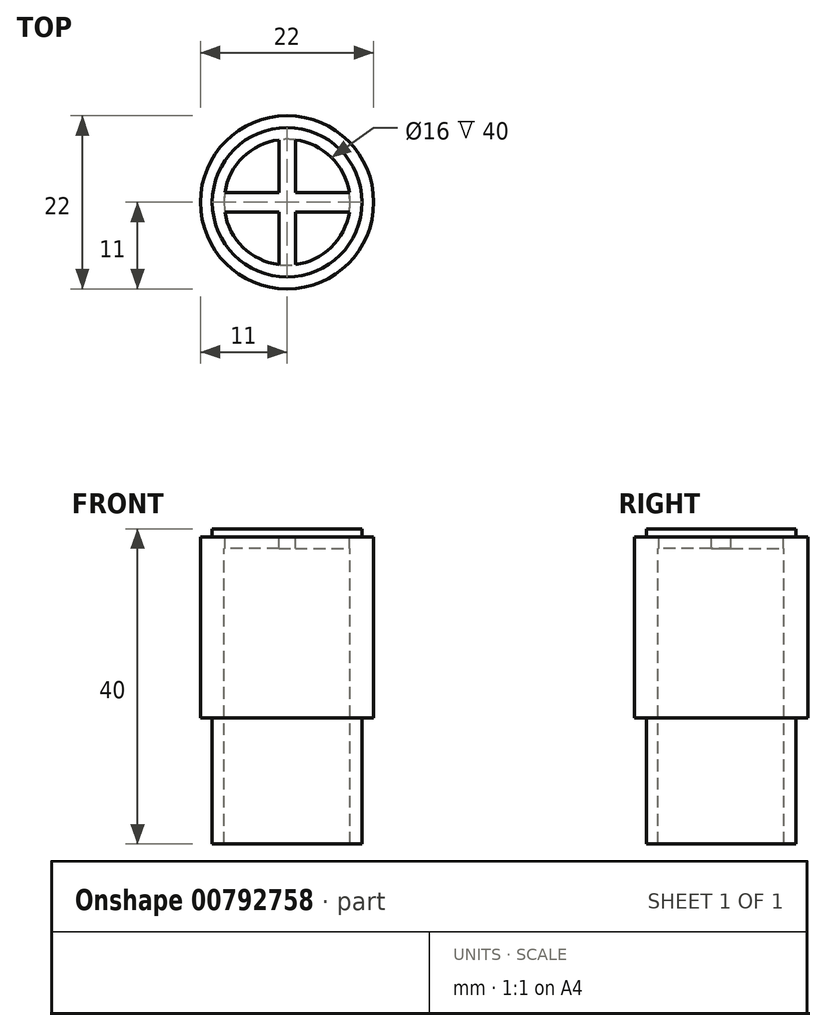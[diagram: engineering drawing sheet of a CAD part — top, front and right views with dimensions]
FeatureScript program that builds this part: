
annotation { "Feature Type Name" : "Feature", "Feature Type Description" : "" }
export const myFeature = defineFeature(function(context is Context, id is Id, definition is map)
    precondition{}
    {
        {
            var Q0;
            Q0=qCreatedBy(makeId("Top.planeOp"),FACE);
            var sketch = newSketch(context, id + "F0", { "sketchPlane" : qUnion([Q0])});
            skCircle(sketch, "E0", {"center": v(0, 0) * mm, "radius": 9.5 * mm});
            skSolve(sketch);
        }
        {
            var Q0;
            Q0 = qSketchRegion(id + "F0", true);
            extrude(context, id + "F1", {"entities" : qUnion([Q0]), "endBound" : BoundingType.SYMMETRIC, "depth" : 40 * mm, "offsetDistance" : 25 * mm});
        }
        {
            var Q0;
            Q0=makeQuery(id+"F1.opExtrude","CAP_FACE",FACE,{"disambiguationData":[OSD([sQuery(id+"F0.wireOp",EDGE,"E0")])],"isStart":false});
            var sketch = newSketch(context, id + "F2", { "sketchPlane" : qUnion([Q0])});
            skCircle(sketch, "E1", {"center": v(0, 0) * mm, "radius": 8 * mm});
            skCircle(sketch, "E2", {"center": v(0, 0) * mm, "radius": 1.63 * mm});
            skLineSegment(sketch, "E3", {"start": v(-1.05, 1.24) * mm, "end": v(-1.05, 7.93) * mm});
            skLineSegment(sketch, "E4", {"start": v(1.05, 1.24) * mm, "end": v(1.05, 7.93) * mm});
            skLineSegment(sketch, "E5", {"start": v(1.05, 1.24) * mm, "end": v(7.9, 1.24) * mm});
            skLineSegment(sketch, "E6", {"start": v(1.05, -1.24) * mm, "end": v(7.9, -1.24) * mm});
            skLineSegment(sketch, "E7", {"start": v(1.05, -1.24) * mm, "end": v(1.05, -7.93) * mm});
            skLineSegment(sketch, "E8", {"start": v(-1.05, -1.24) * mm, "end": v(-1.05, -7.93) * mm});
            skLineSegment(sketch, "E9", {"start": v(-1.05, 1.24) * mm, "end": v(-7.9, 1.24) * mm});
            skLineSegment(sketch, "E10", {"start": v(-1.05, -1.24) * mm, "end": v(-7.9, -1.24) * mm});
            skSolve(sketch);
        }
        {
            var Q0;
            {var subQ0=sQuery(id+"F2.wireOp",EDGE,"E3");Q0=makeQuery(id+"F2.imprint","IMPRINT",FACE,{"disambiguationData":[TD([[makeQuery(id+"F2.imprint","IMPRINT",EDGE,{"derivedFrom":subQ0}),1.0]])]});}
            var Q1;
            {var subQ0=sQuery(id+"F2.wireOp",EDGE,"E4");Q1=makeQuery(id+"F2.imprint","IMPRINT",FACE,{"disambiguationData":[TD([[makeQuery(id+"F2.imprint","IMPRINT",EDGE,{"derivedFrom":subQ0}),-1.0]])]});}
            var Q2;
            {var subQ0=sQuery(id+"F2.wireOp",EDGE,"E6");Q2=makeQuery(id+"F2.imprint","IMPRINT",FACE,{"disambiguationData":[TD([[makeQuery(id+"F2.imprint","IMPRINT",EDGE,{"derivedFrom":subQ0}),-1.0]])]});}
            var Q3;
            {var subQ0=sQuery(id+"F2.wireOp",EDGE,"E8");Q3=makeQuery(id+"F2.imprint","IMPRINT",FACE,{"disambiguationData":[TD([[makeQuery(id+"F2.imprint","IMPRINT",EDGE,{"derivedFrom":subQ0}),-1.0]])]});}
            extrude(context, id + "F3", {"entities" : qUnion([Q0, Q1, Q2, Q3]), "operationType" : NewBodyOperationType.REMOVE, "oppositeDirection" : true, "depth" : 50 * mm, "offsetDistance" : 25 * mm});
        }
        {
            var Q0;
            Q0=makeQuery(id+"F1.opExtrude","CAP_FACE",FACE,{"disambiguationData":[OSD([sQuery(id+"F0.wireOp",EDGE,"E0")])],"isStart":false});
            var sketch = newSketch(context, id + "F4", { "sketchPlane" : qUnion([Q0])});
            skLineSegment(sketch, "E11", {"start": v(-1.05, 1.24) * mm, "end": v(-1.05, 7.93) * mm});
            skLineSegment(sketch, "E12", {"start": v(1.05, 1.24) * mm, "end": v(1.05, 7.93) * mm});
            skLineSegment(sketch, "E13", {"start": v(1.05, 1.24) * mm, "end": v(7.9, 1.24) * mm});
            skLineSegment(sketch, "E14", {"start": v(1.05, -1.24) * mm, "end": v(7.9, -1.24) * mm});
            skLineSegment(sketch, "E15", {"start": v(1.05, -1.24) * mm, "end": v(1.05, -7.93) * mm});
            skLineSegment(sketch, "E16", {"start": v(-1.05, -1.24) * mm, "end": v(-1.05, -7.93) * mm});
            skLineSegment(sketch, "E17", {"start": v(-1.05, -1.24) * mm, "end": v(-7.9, -1.24) * mm});
            skLineSegment(sketch, "E18", {"start": v(-1.05, 1.24) * mm, "end": v(-7.9, 1.24) * mm});
            skCircle(sketch, "E19", {"center": v(0, 0) * mm, "radius": 1.63 * mm});
            skCircle(sketch, "E20", {"center": v(0, 0) * mm, "radius": 8 * mm});
            skSolve(sketch);
        }
        {
            var Q0;
            Q0 = qSketchRegion(id + "F4", true);
            var Q1;
            {var subQ0=sQuery(id+"F2.wireOp",EDGE,"E2");var subQ1=makeQuery(id+"F2.imprint","INTERSECT",VERTEX,{"derivedFrom":[subQ0,sQuery(id+"F2.wireOp",EDGE,"E3"),sQuery(id+"F2.wireOp",EDGE,"E9")]});Q1=makeQuery(id+"F2.imprint","IMPRINT",FACE,{"disambiguationData":[TD([[makeQuery(id+"F2.imprint","IMPRINT",EDGE,{"disambiguationData":[TD([[subQ1,1.0]])],"derivedFrom":subQ0}),1.0]])]});}
            extrude(context, id + "F5", {"entities" : qUnion([Q0, Q1]), "operationType" : NewBodyOperationType.REMOVE, "oppositeDirection" : true, "depth" : 50 * mm, "offsetDistance" : 25 * mm});
        }
        {
            var Q0;
            Q0=makeQuery(id+"F2.imprint","IMPRINT",FACE,{"disambiguationData":[TD([[makeQuery(id+"F2.imprint","IMPRINT",EDGE,{"derivedFrom":makeQuery(id+"F1.opExtrude","CAP_EDGE",EDGE,{"disambiguationData":[OSD([sQuery(id+"F0.wireOp",EDGE,"E0")])],"isStart":false})}),1.0]])]});
            var sketch = newSketch(context, id + "F6", { "sketchPlane" : qUnion([Q0])});
            skLineSegment(sketch, "E21", {"start": v(-1.05, 1.24) * mm, "end": v(-1.05, 7.93) * mm});
            skLineSegment(sketch, "E22", {"start": v(1.05, 1.24) * mm, "end": v(1.05, 7.93) * mm});
            skLineSegment(sketch, "E23", {"start": v(-1.05, 1.24) * mm, "end": v(-7.9, 1.24) * mm});
            skLineSegment(sketch, "E24", {"start": v(-1.05, -1.24) * mm, "end": v(-7.9, -1.24) * mm});
            skLineSegment(sketch, "E25", {"start": v(-1.05, -1.24) * mm, "end": v(-1.05, -7.93) * mm});
            skLineSegment(sketch, "E26", {"start": v(1.05, -1.24) * mm, "end": v(1.05, -7.93) * mm});
            skLineSegment(sketch, "E27", {"start": v(1.05, -1.24) * mm, "end": v(7.9, -1.24) * mm});
            skLineSegment(sketch, "E28", {"start": v(1.05, 1.24) * mm, "end": v(7.9, 1.24) * mm});
            skCircle(sketch, "E29", {"center": v(0, 0) * mm, "radius": 1.63 * mm});
            skArc(sketch, "E30", {"start": v(1.05, 7.93) * mm, "mid": v(0, 8) * mm, "end": v(-1.05, 7.93) * mm});
            skArc(sketch, "E31", {"start": v(7.9, -1.24) * mm, "mid": v(8, 0) * mm, "end": v(7.9, 1.24) * mm});
            skArc(sketch, "E32", {"start": v(-1.05, -7.93) * mm, "mid": v(0, -8) * mm, "end": v(1.05, -7.93) * mm});
            skArc(sketch, "E33", {"start": v(-7.9, 1.24) * mm, "mid": v(-8, 0) * mm, "end": v(-7.9, -1.24) * mm});
            skSolve(sketch);
        }
        {
            var Q0;
            Q0 = qSketchRegion(id + "F6", true);
            extrude(context, id + "F7", {"entities" : qUnion([Q0]), "operationType" : NewBodyOperationType.ADD, "oppositeDirection" : true, "depth" : 2.5 * mm, "offsetDistance" : 25 * mm});
        }
        {
            var Q0;
            Q0=makeQuery(id+"F1.opExtrude","CAP_FACE",FACE,{"disambiguationData":[OSD([sQuery(id+"F0.wireOp",EDGE,"E0")])],"isStart":true});
            var sketch = newSketch(context, id + "F8", { "sketchPlane" : qUnion([Q0])});
            skCircle(sketch, "E34", {"center": v(0, 0) * mm, "radius": 11 * mm});
            skCircle(sketch, "E35", {"center": v(0, 0) * mm, "radius": 9.5 * mm});
            skSolve(sketch);
        }
        {
            var Q0;
            Q0=makeQuery(id+"F8.imprint","IMPRINT",FACE,{"disambiguationData":[TD([[makeQuery(id+"F8.imprint","IMPRINT",EDGE,{"derivedFrom":sQuery(id+"F8.wireOp",EDGE,"E34")}),1.0]])]});
            extrude(context, id + "F9", {"entities" : qUnion([Q0]), "operationType" : NewBodyOperationType.ADD, "oppositeDirection" : true, "depth" : 39 * mm, "offsetDistance" : 25 * mm});
        }
        {
            var Q0;
            Q0=makeQuery(id+"F9.boolean.opBoolean","MERGE",FACE,{"derivedFrom":[makeQuery(id+"F1.opExtrude","CAP_FACE",FACE,{"disambiguationData":[OSD([sQuery(id+"F0.wireOp",EDGE,"E0")])],"isStart":true}),makeQuery(id+"F9.opExtrude","CAP_FACE",FACE,{"disambiguationData":[OSD([sQuery(id+"F8.wireOp",EDGE,"E34"),sQuery(id+"F8.wireOp",EDGE,"E35")])],"isStart":true})]});
            var sketch = newSketch(context, id + "F10", { "sketchPlane" : qUnion([Q0])});
            skCircle(sketch, "E36", {"center": v(0, 0) * mm, "radius": 9.5 * mm});
            skCircle(sketch, "E37", {"center": v(0, 0) * mm, "radius": 11 * mm});
            skSolve(sketch);
        }
        {
            var Q0;
            Q0 = qSketchRegion(id + "F10", true);
            extrude(context, id + "F11", {"entities" : qUnion([Q0]), "operationType" : NewBodyOperationType.REMOVE, "oppositeDirection" : true, "depth" : 16 * mm, "offsetDistance" : 25 * mm});
        }
    });
